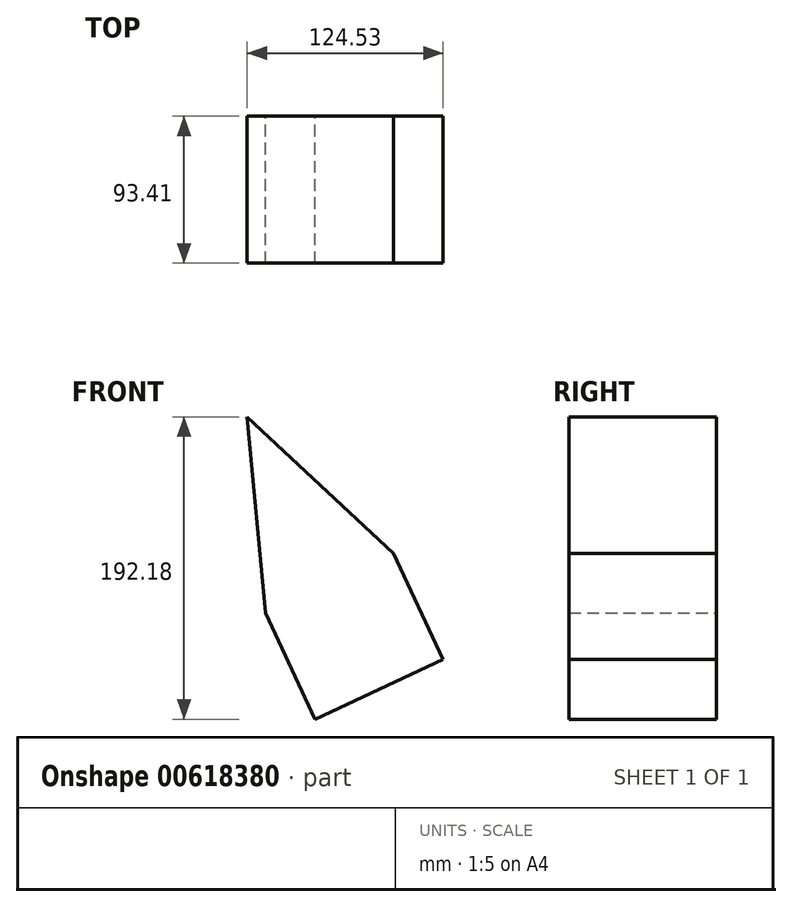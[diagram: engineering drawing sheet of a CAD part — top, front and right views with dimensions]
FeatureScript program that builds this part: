
annotation { "Feature Type Name" : "Feature", "Feature Type Description" : "" }
export const myFeature = defineFeature(function(context is Context, id is Id, definition is map)
    precondition{}
    {
        {
            var Q0;
            Q0=qCreatedBy(makeId("Front.planeOp"),FACE);
            var sketch = newSketch(context, id + "F0", { "sketchPlane" : qUnion([Q0])});
            skLineSegment(sketch, "E0", {"start": v(-47.66, 49.7) * mm, "end": v(45.34, -36.99) * mm});
            skLineSegment(sketch, "E1", {"start": v(45.34, -36.99) * mm, "end": v(-36.07, -75.07) * mm});
            skLineSegment(sketch, "E2", {"start": v(-36.07, -75.07) * mm, "end": v(-47.66, 49.7) * mm});
            skSolve(sketch);
        }
        {
            var Q0;
            Q0=makeQuery(id+"F0.imprint","IMPRINT",FACE,{"disambiguationData":[TD([[makeQuery(id+"F0.imprint","IMPRINT",EDGE,{"derivedFrom":sQuery(id+"F0.wireOp",EDGE,"E0")}),-1.0]])]});
            extrude(context, id + "F1", {"entities" : qUnion([Q0]), "depth" : 93.4 * mm, "offsetDistance" : 25.4 * mm});
        }
        {
            var Q0;
            Q0=makeQuery(id+"F1.opExtrude","SWEPT_FACE",FACE,{"disambiguationData":[OSD([sQuery(id+"F0.wireOp",EDGE,"E1")])]});
            var sketch = newSketch(context, id + "F2", { "sketchPlane" : qUnion([Q0])});
            skSolve(sketch);
        }
        {
            var Q0;
            {var subQ0=sQuery(id+"F0.wireOp",EDGE,"E1");Q0=makeQuery(id+"F2.imprint","IMPRINT",FACE,{"disambiguationData":[TD([[makeQuery(id+"F2.imprint","IMPRINT",EDGE,{"derivedFrom":makeQuery(id+"F1.opExtrude","CAP_EDGE",EDGE,{"disambiguationData":[OSD([subQ0])],"isStart":true})}),-1.0]])]});}
            extrude(context, id + "F3", {"entities" : qUnion([Q0]), "operationType" : NewBodyOperationType.ADD, "depth" : 74.43 * mm, "offsetDistance" : 25.4 * mm});
        }
    });
